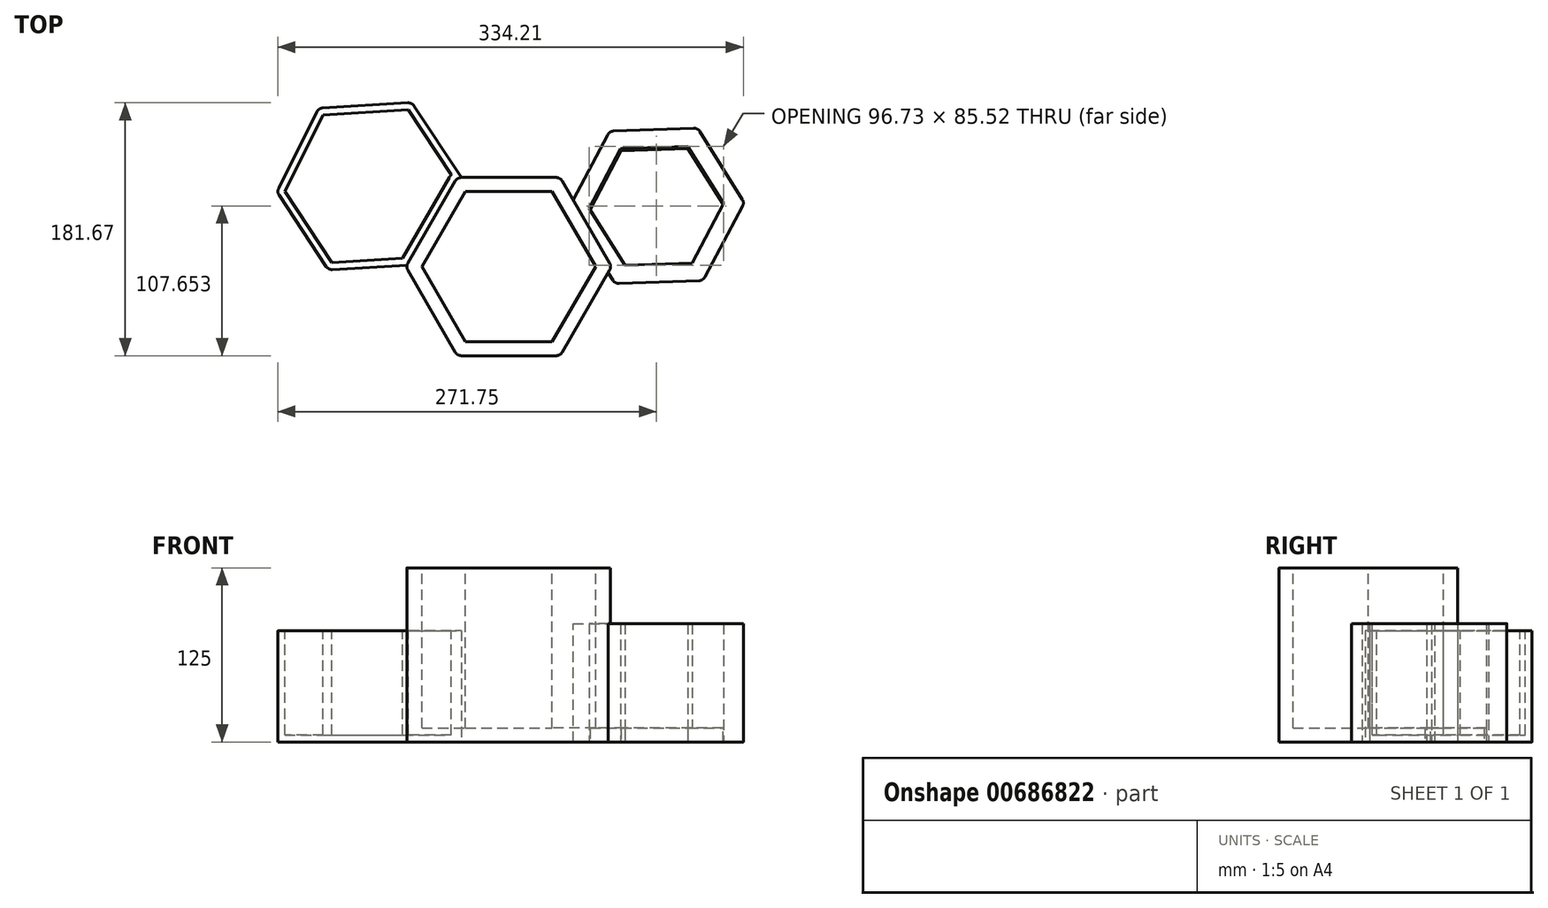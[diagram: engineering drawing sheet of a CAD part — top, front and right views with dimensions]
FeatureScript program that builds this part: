
annotation { "Feature Type Name" : "Feature", "Feature Type Description" : "" }
export const myFeature = defineFeature(function(context is Context, id is Id, definition is map)
    precondition{}
    {
        {
            var Q0;
            Q0=qCreatedBy(makeId("Top.planeOp"),FACE);
            var sketch = newSketch(context, id + "F0", { "sketchPlane" : qUnion([Q0])});
            skCircle(sketch, "E0.cCircle", {"center": v(0, 0) * mm, "radius": 64 * mm, "construction": true});
            skLineSegment(sketch, "E0.0", {"start": v(-36.95, 64) * mm, "end": v(36.95, 64) * mm});
            skLineSegment(sketch, "E0.1", {"start": v(36.95, 64) * mm, "end": v(73.9, 0) * mm});
            skLineSegment(sketch, "E0.2", {"start": v(73.9, 0) * mm, "end": v(36.95, -64) * mm});
            skLineSegment(sketch, "E0.3", {"start": v(36.95, -64) * mm, "end": v(-36.95, -64) * mm});
            skLineSegment(sketch, "E0.4", {"start": v(-36.95, -64) * mm, "end": v(-73.9, 0) * mm});
            skLineSegment(sketch, "E0.5", {"start": v(-73.9, 0) * mm, "end": v(-36.95, 64) * mm});
            skPoint(sketch, "E0.0.midPoint", {"position": v(0, 64) * mm});
            skSolve(sketch);
        }
        {
            var Q0;
            Q0=makeQuery(id+"F0.imprint","IMPRINT",FACE,{"disambiguationData":[TD([[makeQuery(id+"F0.imprint","IMPRINT",EDGE,{"derivedFrom":sQuery(id+"F0.wireOp",EDGE,"E0.0")}),-1.0]])]});
            extrude(context, id + "F1", {"entities" : qUnion([Q0]), "depth" : 100 * mm, "offsetDistance" : 25 * mm});
        }
        {
            var Q0;
            Q0=makeQuery(id+"F1.opExtrude","CAP_FACE",FACE,{"disambiguationData":[OSD([sQuery(id+"F0.wireOp",EDGE,"E0.0"),sQuery(id+"F0.wireOp",EDGE,"E0.1"),sQuery(id+"F0.wireOp",EDGE,"E0.2"),sQuery(id+"F0.wireOp",EDGE,"E0.3"),sQuery(id+"F0.wireOp",EDGE,"E0.4"),sQuery(id+"F0.wireOp",EDGE,"E0.5")])],"isStart":false});
            var sketch = newSketch(context, id + "F2", { "sketchPlane" : qUnion([Q0])});
            skCircle(sketch, "E1.cCircle", {"center": v(0, 0) * mm, "radius": 54 * mm, "construction": true});
            skLineSegment(sketch, "E1.0", {"start": v(-31.18, 54) * mm, "end": v(31.18, 54) * mm});
            skLineSegment(sketch, "E1.1", {"start": v(31.18, 54) * mm, "end": v(62.36, 0) * mm});
            skLineSegment(sketch, "E1.2", {"start": v(62.36, 0) * mm, "end": v(31.18, -54) * mm});
            skLineSegment(sketch, "E1.3", {"start": v(31.18, -54) * mm, "end": v(-31.18, -54) * mm});
            skLineSegment(sketch, "E1.4", {"start": v(-31.18, -54) * mm, "end": v(-62.36, 0) * mm});
            skLineSegment(sketch, "E1.5", {"start": v(-62.36, 0) * mm, "end": v(-31.18, 54) * mm});
            skPoint(sketch, "E1.0.midPoint", {"position": v(0, 54) * mm});
            skSolve(sketch);
        }
        {
            var Q0;
            Q0=makeQuery(id+"F2.imprint","IMPRINT",FACE,{"disambiguationData":[TD([[makeQuery(id+"F2.imprint","IMPRINT",EDGE,{"derivedFrom":sQuery(id+"F2.wireOp",EDGE,"E1.0")}),-1.0]])]});
            extrude(context, id + "F3", {"entities" : qUnion([Q0]), "operationType" : NewBodyOperationType.REMOVE, "oppositeDirection" : true, "depth" : 90 * mm, "offsetDistance" : 25 * mm});
        }
        {
            var Q0;
            Q0=makeQuery(id+"F1.opExtrude","CAP_FACE",FACE,{"disambiguationData":[OSD([sQuery(id+"F0.wireOp",EDGE,"E0.0"),sQuery(id+"F0.wireOp",EDGE,"E0.1"),sQuery(id+"F0.wireOp",EDGE,"E0.2"),sQuery(id+"F0.wireOp",EDGE,"E0.3"),sQuery(id+"F0.wireOp",EDGE,"E0.4"),sQuery(id+"F0.wireOp",EDGE,"E0.5")])],"isStart":false});
            extrude(context, id + "F4", {"entities" : qUnion([Q0]), "operationType" : NewBodyOperationType.ADD, "depth" : 25 * mm, "offsetDistance" : 25 * mm});
        }
        {
            var Q0;
            {var subQ0=sQuery(id+"F0.wireOp",EDGE,"E0.3");var subQ1=sQuery(id+"F0.wireOp",EDGE,"E0.2");Q0=makeQuery(id+"F4.boolean.opBoolean","MERGE",EDGE,{"derivedFrom":[makeQuery(id+"F1.opExtrude","SWEPT_EDGE",EDGE,{"disambiguationData":[OSD([subQ1,subQ0])]}),makeQuery(id+"F4.opExtrude","SWEPT_EDGE",EDGE,{"disambiguationData":[OSD([subQ1,subQ0])]})]});}
            var Q1;
            {var subQ0=sQuery(id+"F0.wireOp",EDGE,"E0.2");var subQ1=sQuery(id+"F0.wireOp",EDGE,"E0.1");Q1=makeQuery(id+"F4.boolean.opBoolean","MERGE",EDGE,{"derivedFrom":[makeQuery(id+"F1.opExtrude","SWEPT_EDGE",EDGE,{"disambiguationData":[OSD([subQ1,subQ0])]}),makeQuery(id+"F4.opExtrude","SWEPT_EDGE",EDGE,{"disambiguationData":[OSD([subQ1,subQ0])]})]});}
            var Q2;
            {var subQ0=sQuery(id+"F0.wireOp",EDGE,"E0.1");var subQ1=sQuery(id+"F0.wireOp",EDGE,"E0.0");Q2=makeQuery(id+"F4.boolean.opBoolean","MERGE",EDGE,{"derivedFrom":[makeQuery(id+"F1.opExtrude","SWEPT_EDGE",EDGE,{"disambiguationData":[OSD([subQ1,subQ0])]}),makeQuery(id+"F4.opExtrude","SWEPT_EDGE",EDGE,{"disambiguationData":[OSD([subQ1,subQ0])]})]});}
            var Q3;
            {var subQ0=sQuery(id+"F0.wireOp",EDGE,"E0.4");var subQ1=sQuery(id+"F0.wireOp",EDGE,"E0.3");Q3=makeQuery(id+"F4.boolean.opBoolean","MERGE",EDGE,{"derivedFrom":[makeQuery(id+"F1.opExtrude","SWEPT_EDGE",EDGE,{"disambiguationData":[OSD([subQ1,subQ0])]}),makeQuery(id+"F4.opExtrude","SWEPT_EDGE",EDGE,{"disambiguationData":[OSD([subQ1,subQ0])]})]});}
            var Q4;
            {var subQ0=sQuery(id+"F0.wireOp",EDGE,"E0.5");var subQ1=sQuery(id+"F0.wireOp",EDGE,"E0.4");Q4=makeQuery(id+"F4.boolean.opBoolean","MERGE",EDGE,{"derivedFrom":[makeQuery(id+"F1.opExtrude","SWEPT_EDGE",EDGE,{"disambiguationData":[OSD([subQ1,subQ0])]}),makeQuery(id+"F4.opExtrude","SWEPT_EDGE",EDGE,{"disambiguationData":[OSD([subQ1,subQ0])]})]});}
            var Q5;
            {var subQ0=sQuery(id+"F0.wireOp",EDGE,"E0.5");var subQ1=sQuery(id+"F0.wireOp",EDGE,"E0.0");Q5=makeQuery(id+"F4.boolean.opBoolean","MERGE",EDGE,{"derivedFrom":[makeQuery(id+"F1.opExtrude","SWEPT_EDGE",EDGE,{"disambiguationData":[OSD([subQ1,subQ0])]}),makeQuery(id+"F4.opExtrude","SWEPT_EDGE",EDGE,{"disambiguationData":[OSD([subQ1,subQ0])]})]});}
            fillet(context, id + "F5", {"entities" : qUnion([Q0, Q1, Q2, Q3, Q4, Q5]), "radius" : 5 * mm, "tangentPropagation" : true, "allowEdgeOverflow" : false});
        }
        {
            var Q0;
            Q0=qCreatedBy(makeId("Top.planeOp"),FACE);
            var sketch = newSketch(context, id + "F6", { "sketchPlane" : qUnion([Q0])});
            skCircle(sketch, "E2.cCircle", {"center": v(105.99, 43.64) * mm, "radius": 54.8 * mm, "construction": true});
            skLineSegment(sketch, "E2.0", {"start": v(42.76, 41.37) * mm, "end": v(72.4, 97.26) * mm});
            skLineSegment(sketch, "E2.1", {"start": v(72.4, 97.26) * mm, "end": v(135.63, 99.54) * mm});
            skLineSegment(sketch, "E2.2", {"start": v(135.63, 99.54) * mm, "end": v(169.22, 45.92) * mm});
            skLineSegment(sketch, "E2.3", {"start": v(169.22, 45.92) * mm, "end": v(139.58, -9.98) * mm});
            skLineSegment(sketch, "E2.4", {"start": v(139.58, -9.98) * mm, "end": v(76.35, -12.26) * mm});
            skLineSegment(sketch, "E2.5", {"start": v(76.35, -12.26) * mm, "end": v(42.76, 41.37) * mm});
            skPoint(sketch, "E2.0.midPoint", {"position": v(57.58, 69.32) * mm});
            skCircle(sketch, "E3.cCircle", {"center": v(105.99, 43.64) * mm, "radius": 41.91 * mm, "construction": true});
            skLineSegment(sketch, "E3.0", {"start": v(80.3, 84.66) * mm, "end": v(128.66, 86.4) * mm});
            skLineSegment(sketch, "E3.1", {"start": v(128.66, 86.4) * mm, "end": v(154.36, 45.38) * mm});
            skLineSegment(sketch, "E3.2", {"start": v(154.36, 45.38) * mm, "end": v(131.68, 2.63) * mm});
            skLineSegment(sketch, "E3.3", {"start": v(131.68, 2.63) * mm, "end": v(83.32, 0.88) * mm});
            skLineSegment(sketch, "E3.4", {"start": v(83.32, 0.88) * mm, "end": v(57.62, 41.9) * mm});
            skLineSegment(sketch, "E3.5", {"start": v(57.62, 41.9) * mm, "end": v(80.3, 84.66) * mm});
            skPoint(sketch, "E3.0.midPoint", {"position": v(104.48, 85.53) * mm});
            skSolve(sketch);
        }
        {
            var Q0;
            Q0 = qSketchRegion(id + "F6", true);
            extrude(context, id + "F7", {"entities" : qUnion([Q0]), "operationType" : NewBodyOperationType.ADD, "depth" : 25 * mm, "offsetDistance" : 25 * mm});
        }
        {
            var Q0;
            Q0=makeQuery(id+"F7.opExtrude","CAP_FACE",FACE,{"disambiguationData":[OSD([sQuery(id+"F6.wireOp",EDGE,"E2.0"),sQuery(id+"F6.wireOp",EDGE,"E2.1"),sQuery(id+"F6.wireOp",EDGE,"E2.2"),sQuery(id+"F6.wireOp",EDGE,"E2.3"),sQuery(id+"F6.wireOp",EDGE,"E2.4"),sQuery(id+"F6.wireOp",EDGE,"E2.5"),sQuery(id+"F6.wireOp",EDGE,"E3.0"),sQuery(id+"F6.wireOp",EDGE,"E3.1"),sQuery(id+"F6.wireOp",EDGE,"E3.2"),sQuery(id+"F6.wireOp",EDGE,"E3.3"),sQuery(id+"F6.wireOp",EDGE,"E3.4"),sQuery(id+"F6.wireOp",EDGE,"E3.5")])],"isStart":false});
            extrude(context, id + "F8", {"entities" : qUnion([Q0]), "operationType" : NewBodyOperationType.ADD, "depth" : 60 * mm, "offsetDistance" : 25 * mm});
        }
        {
            var Q0;
            {var subQ0=sQuery(id+"F6.wireOp",EDGE,"E2.4");var subQ1=sQuery(id+"F6.wireOp",EDGE,"E2.3");Q0=makeQuery(id+"F8.boolean.opBoolean","MERGE",EDGE,{"derivedFrom":[makeQuery(id+"F7.opExtrude","SWEPT_EDGE",EDGE,{"disambiguationData":[OSD([subQ1,subQ0])]}),makeQuery(id+"F8.opExtrude","SWEPT_EDGE",EDGE,{"disambiguationData":[OSD([subQ1,subQ0])]})]});}
            var Q1;
            {var subQ0=sQuery(id+"F6.wireOp",EDGE,"E2.3");var subQ1=sQuery(id+"F6.wireOp",EDGE,"E2.2");Q1=makeQuery(id+"F8.boolean.opBoolean","MERGE",EDGE,{"derivedFrom":[makeQuery(id+"F7.opExtrude","SWEPT_EDGE",EDGE,{"disambiguationData":[OSD([subQ1,subQ0])]}),makeQuery(id+"F8.opExtrude","SWEPT_EDGE",EDGE,{"disambiguationData":[OSD([subQ1,subQ0])]})]});}
            var Q2;
            {var subQ0=sQuery(id+"F6.wireOp",EDGE,"E2.2");var subQ1=sQuery(id+"F6.wireOp",EDGE,"E2.1");Q2=makeQuery(id+"F8.boolean.opBoolean","MERGE",EDGE,{"derivedFrom":[makeQuery(id+"F7.opExtrude","SWEPT_EDGE",EDGE,{"disambiguationData":[OSD([subQ1,subQ0])]}),makeQuery(id+"F8.opExtrude","SWEPT_EDGE",EDGE,{"disambiguationData":[OSD([subQ1,subQ0])]})]});}
            var Q3;
            {var subQ0=sQuery(id+"F6.wireOp",EDGE,"E2.5");var subQ1=sQuery(id+"F6.wireOp",EDGE,"E2.4");Q3=makeQuery(id+"F8.boolean.opBoolean","MERGE",EDGE,{"derivedFrom":[makeQuery(id+"F7.opExtrude","SWEPT_EDGE",EDGE,{"disambiguationData":[OSD([subQ1,subQ0])]}),makeQuery(id+"F8.opExtrude","SWEPT_EDGE",EDGE,{"disambiguationData":[OSD([subQ1,subQ0])]})]});}
            var Q4;
            {var subQ0=sQuery(id+"F6.wireOp",EDGE,"E2.1");var subQ1=sQuery(id+"F6.wireOp",EDGE,"E2.0");Q4=makeQuery(id+"F8.boolean.opBoolean","MERGE",EDGE,{"derivedFrom":[makeQuery(id+"F7.opExtrude","SWEPT_EDGE",EDGE,{"disambiguationData":[OSD([subQ1,subQ0])]}),makeQuery(id+"F8.opExtrude","SWEPT_EDGE",EDGE,{"disambiguationData":[OSD([subQ1,subQ0])]})]});}
            fillet(context, id + "F9", {"entities" : qUnion([Q0, Q1, Q2, Q3, Q4]), "radius" : 5 * mm, "tangentPropagation" : true, "allowEdgeOverflow" : false});
        }
        {
            var Q0;
            Q0=makeQuery(id+"F8.opExtrude","CAP_FACE",FACE,{"disambiguationData":[OSD([sQuery(id+"F6.wireOp",EDGE,"E2.0"),sQuery(id+"F6.wireOp",EDGE,"E2.1"),sQuery(id+"F6.wireOp",EDGE,"E2.2"),sQuery(id+"F6.wireOp",EDGE,"E2.3"),sQuery(id+"F6.wireOp",EDGE,"E2.4"),sQuery(id+"F6.wireOp",EDGE,"E2.5"),sQuery(id+"F6.wireOp",EDGE,"E3.0"),sQuery(id+"F6.wireOp",EDGE,"E3.1"),sQuery(id+"F6.wireOp",EDGE,"E3.2"),sQuery(id+"F6.wireOp",EDGE,"E3.3"),sQuery(id+"F6.wireOp",EDGE,"E3.4"),sQuery(id+"F6.wireOp",EDGE,"E3.5")])],"isStart":false});
            var sketch = newSketch(context, id + "F10", { "sketchPlane" : qUnion([Q0])});
            skSolve(sketch);
        }
        {
            var Q0;
            Q0=makeQuery(id+"F10.imprint","IMPRINT",FACE,{"disambiguationData":[TD([[makeQuery(id+"F10.imprint","IMPRINT",EDGE,{"derivedFrom":makeQuery(id+"F8.opExtrude","CAP_EDGE",EDGE,{"disambiguationData":[OSD([sQuery(id+"F6.wireOp",EDGE,"E3.0")])],"isStart":false})}),-1.0]])]});
            extrude(context, id + "F11", {"entities" : qUnion([Q0]), "depth" : 10 * mm, "offsetDistance" : 25 * mm});
        }
        {
            var Q0;
            Q0=makeQuery(id+"F11.opExtrude","CAP_FACE",FACE,{"disambiguationData":[OSD([sQuery(id+"F6.wireOp",EDGE,"E3.0"),sQuery(id+"F6.wireOp",EDGE,"E3.1"),sQuery(id+"F6.wireOp",EDGE,"E3.2"),sQuery(id+"F6.wireOp",EDGE,"E3.3"),sQuery(id+"F6.wireOp",EDGE,"E3.4"),sQuery(id+"F6.wireOp",EDGE,"E3.5")])],"isStart":false});
            extrude(context, id + "F12", {"entities" : qUnion([Q0]), "operationType" : NewBodyOperationType.REMOVE, "oppositeDirection" : true, "depth" : 50 * mm, "offsetDistance" : 25 * mm});
        }
        {
            var Q0;
            Q0=qCreatedBy(makeId("Top.planeOp"),FACE);
            var sketch = newSketch(context, id + "F13", { "sketchPlane" : qUnion([Q0])});
            skCircle(sketch, "E4.cCircle", {"center": v(106.25, 42.55) * mm, "radius": 41.49 * mm, "construction": true});
            skLineSegment(sketch, "E4.0", {"start": v(58.38, 40.73) * mm, "end": v(80.74, 83.1) * mm});
            skLineSegment(sketch, "E4.1", {"start": v(80.74, 83.1) * mm, "end": v(128.61, 84.92) * mm});
            skLineSegment(sketch, "E4.2", {"start": v(128.61, 84.92) * mm, "end": v(154.12, 44.37) * mm});
            skLineSegment(sketch, "E4.3", {"start": v(154.12, 44.37) * mm, "end": v(131.76, 2) * mm});
            skLineSegment(sketch, "E4.4", {"start": v(131.76, 2) * mm, "end": v(83.89, 0.18) * mm});
            skLineSegment(sketch, "E4.5", {"start": v(83.89, 0.18) * mm, "end": v(58.38, 40.73) * mm});
            skPoint(sketch, "E4.0.midPoint", {"position": v(69.56, 61.92) * mm});
            skSolve(sketch);
        }
        {
            var Q0;
            Q0 = qSketchRegion(id + "F13", true);
            extrude(context, id + "F14", {"entities" : qUnion([Q0]), "operationType" : NewBodyOperationType.ADD, "depth" : 10 * mm, "offsetDistance" : 25 * mm});
        }
        {
            var Q0;
            Q0=qCreatedBy(makeId("Top.planeOp"),FACE);
            var sketch = newSketch(context, id + "F15", { "sketchPlane" : qUnion([Q0])});
            skCircle(sketch, "E5.cCircle", {"center": v(-99.5, 57.76) * mm, "radius": 58.15 * mm, "construction": true});
            skLineSegment(sketch, "E5.0", {"start": v(-32.46, 61.78) * mm, "end": v(-62.5, 1.72) * mm});
            skLineSegment(sketch, "E5.1", {"start": v(-62.5, 1.72) * mm, "end": v(-129.52, -2.3) * mm});
            skLineSegment(sketch, "E5.2", {"start": v(-129.52, -2.3) * mm, "end": v(-166.52, 53.74) * mm});
            skLineSegment(sketch, "E5.3", {"start": v(-166.52, 53.74) * mm, "end": v(-136.5, 113.8) * mm});
            skLineSegment(sketch, "E5.4", {"start": v(-136.5, 113.8) * mm, "end": v(-69.46, 117.82) * mm});
            skLineSegment(sketch, "E5.5", {"start": v(-69.46, 117.82) * mm, "end": v(-32.46, 61.78) * mm});
            skPoint(sketch, "E5.0.midPoint", {"position": v(-47.48, 31.75) * mm});
            skSolve(sketch);
        }
        {
            var Q0;
            Q0=makeQuery(id+"F15.imprint","IMPRINT",FACE,{"disambiguationData":[TD([[makeQuery(id+"F15.imprint","IMPRINT",EDGE,{"derivedFrom":sQuery(id+"F15.wireOp",EDGE,"E5.0")}),-1.0]])]});
            extrude(context, id + "F16", {"entities" : qUnion([Q0]), "operationType" : NewBodyOperationType.ADD, "depth" : 80 * mm, "offsetDistance" : 25 * mm});
        }
        {
            var Q0;
            Q0=makeQuery(id+"F16.opExtrude","CAP_FACE",FACE,{"disambiguationData":[OSD([sQuery(id+"F15.wireOp",EDGE,"E5.0"),sQuery(id+"F15.wireOp",EDGE,"E5.1"),sQuery(id+"F15.wireOp",EDGE,"E5.2"),sQuery(id+"F15.wireOp",EDGE,"E5.3"),sQuery(id+"F15.wireOp",EDGE,"E5.4"),sQuery(id+"F15.wireOp",EDGE,"E5.5")])],"isStart":false});
            var sketch = newSketch(context, id + "F17", { "sketchPlane" : qUnion([Q0])});
            skLineSegment(sketch, "E6.0", {"start": v(-136.2, 108.8) * mm, "end": v(-69.16, 112.83) * mm});
            skLineSegment(sketch, "E7.0", {"start": v(-168.35, 54.65) * mm, "end": v(-138.32, 114.71) * mm});
            skLineSegment(sketch, "E8.0", {"start": v(-160.76, 54.08) * mm, "end": v(-126.94, 2.86) * mm});
            skLineSegment(sketch, "E8.1", {"start": v(-133.3, 108.98) * mm, "end": v(-160.76, 54.08) * mm});
            skLineSegment(sketch, "E8.2", {"start": v(-76.27, 5.9) * mm, "end": v(-42.73, 64) * mm});
            skArc(sketch, "E8.3", {"start": v(-42.73, 64) * mm, "mid": v(-42.04, 65.04) * mm, "end": v(-41.23, 65.99) * mm});
            skLineSegment(sketch, "E8.4", {"start": v(-41.23, 65.99) * mm, "end": v(-72.04, 112.66) * mm});
            skLineSegment(sketch, "E8.5", {"start": v(-126.94, 2.86) * mm, "end": v(-76.27, 5.9) * mm});
            skLineSegment(sketch, "E8.6", {"start": v(-72.04, 112.66) * mm, "end": v(-133.3, 108.98) * mm});
            skSolve(sketch);
        }
        {
            var Q0;
            Q0=makeQuery(id+"F17.imprint","IMPRINT",FACE,{"disambiguationData":[TD([[makeQuery(id+"F17.imprint","IMPRINT",EDGE,{"derivedFrom":sQuery(id+"F17.wireOp",EDGE,"E8.0")}),1.0]])]});
            extrude(context, id + "F18", {"entities" : qUnion([Q0]), "operationType" : NewBodyOperationType.REMOVE, "oppositeDirection" : true, "depth" : 75 * mm, "offsetDistance" : 25 * mm});
        }
        {
            var Q0;
            Q0=makeQuery(id+"F16.opExtrude","SWEPT_EDGE",EDGE,{"disambiguationData":[OSD([sQuery(id+"F15.wireOp",EDGE,"E5.1"),sQuery(id+"F15.wireOp",EDGE,"E5.2")])]});
            var Q1;
            Q1=makeQuery(id+"F16.opExtrude","SWEPT_EDGE",EDGE,{"disambiguationData":[OSD([sQuery(id+"F15.wireOp",EDGE,"E5.2"),sQuery(id+"F15.wireOp",EDGE,"E5.3")])]});
            var Q2;
            Q2=makeQuery(id+"F16.opExtrude","SWEPT_EDGE",EDGE,{"disambiguationData":[OSD([sQuery(id+"F15.wireOp",EDGE,"E5.3"),sQuery(id+"F15.wireOp",EDGE,"E5.4")])]});
            var Q3;
            Q3=makeQuery(id+"F16.opExtrude","SWEPT_EDGE",EDGE,{"disambiguationData":[OSD([sQuery(id+"F15.wireOp",EDGE,"E5.4"),sQuery(id+"F15.wireOp",EDGE,"E5.5")])]});
            fillet(context, id + "F19", {"entities" : qUnion([Q0, Q1, Q2, Q3]), "radius" : 5 * mm, "tangentPropagation" : true, "allowEdgeOverflow" : false});
        }
    });
